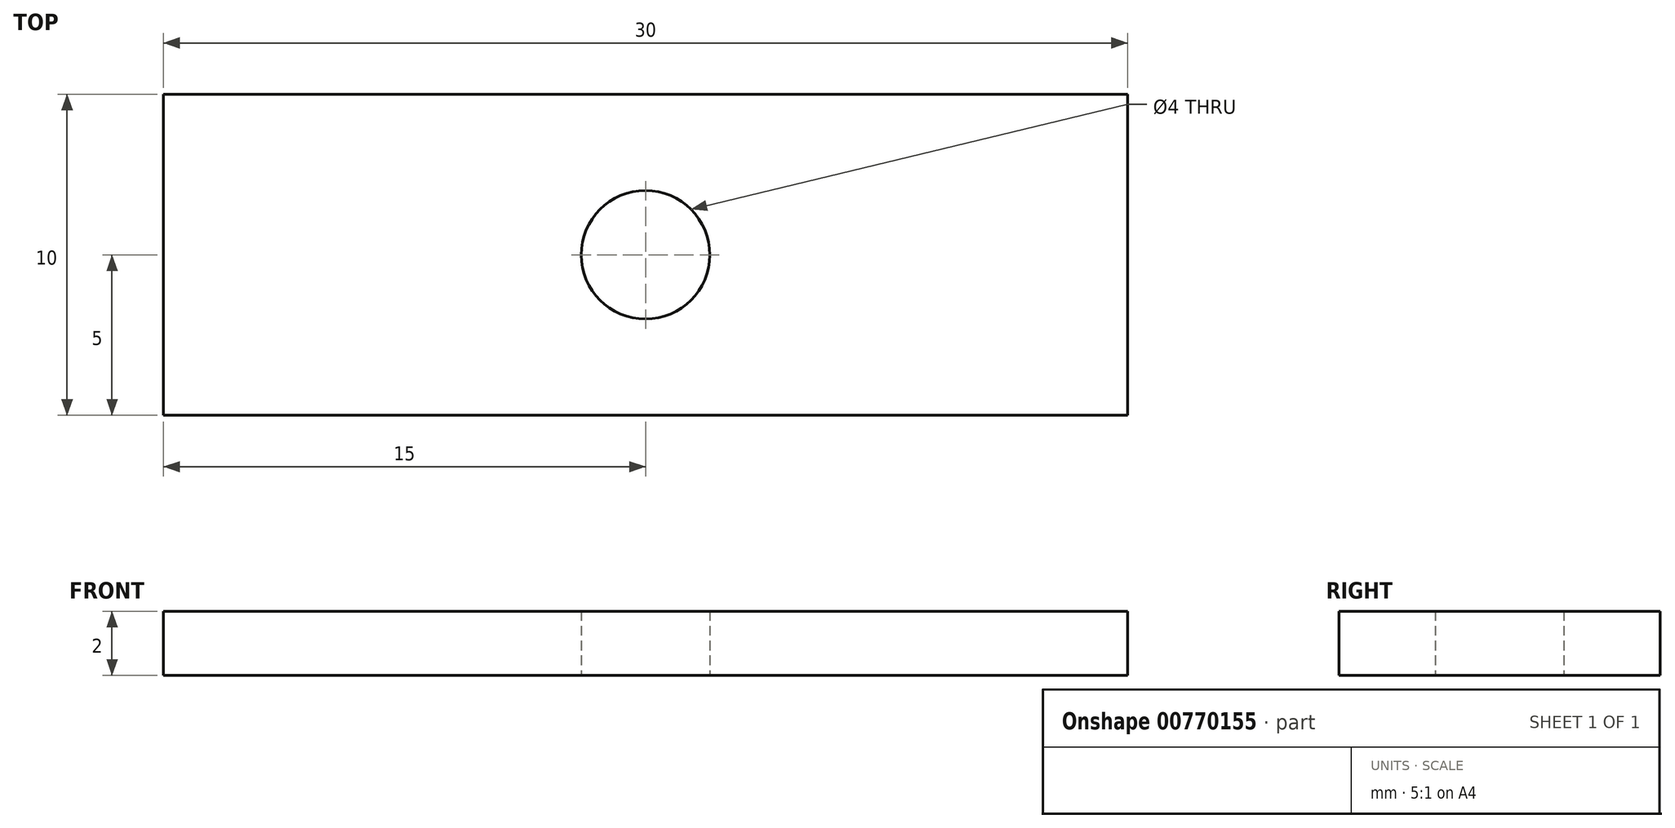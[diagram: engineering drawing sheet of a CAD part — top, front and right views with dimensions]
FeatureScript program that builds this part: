
annotation { "Feature Type Name" : "Feature", "Feature Type Description" : "" }
export const myFeature = defineFeature(function(context is Context, id is Id, definition is map)
    precondition{}
    {
        {
            var Q0;
            Q0=qCreatedBy(makeId("Top.planeOp"),FACE);
            var sketch = newSketch(context, id + "F0", { "sketchPlane" : qUnion([Q0])});
            skLineSegment(sketch, "E0.bottom", {"start": v(-15, 5) * mm, "end": v(15, 5) * mm});
            skLineSegment(sketch, "E0.top", {"start": v(-15, -5) * mm, "end": v(15, -5) * mm});
            skLineSegment(sketch, "E0.left", {"start": v(-15, 5) * mm, "end": v(-15, -5) * mm});
            skLineSegment(sketch, "E0.right", {"start": v(15, 5) * mm, "end": v(15, -5) * mm});
            skPoint(sketch, "E0.middle", {"position": v(0, 0) * mm});
            skCircle(sketch, "E1", {"center": v(0, 0) * mm, "radius": 2 * mm});
            skSolve(sketch);
        }
        {
            var Q0;
            Q0=qSketchRegion(id+"F0",true);
            extrude(context, id + "F1", {"entities" : qUnion([Q0]), "depth" : 2 * mm, "offsetDistance" : 25 * mm});
        }
    });
